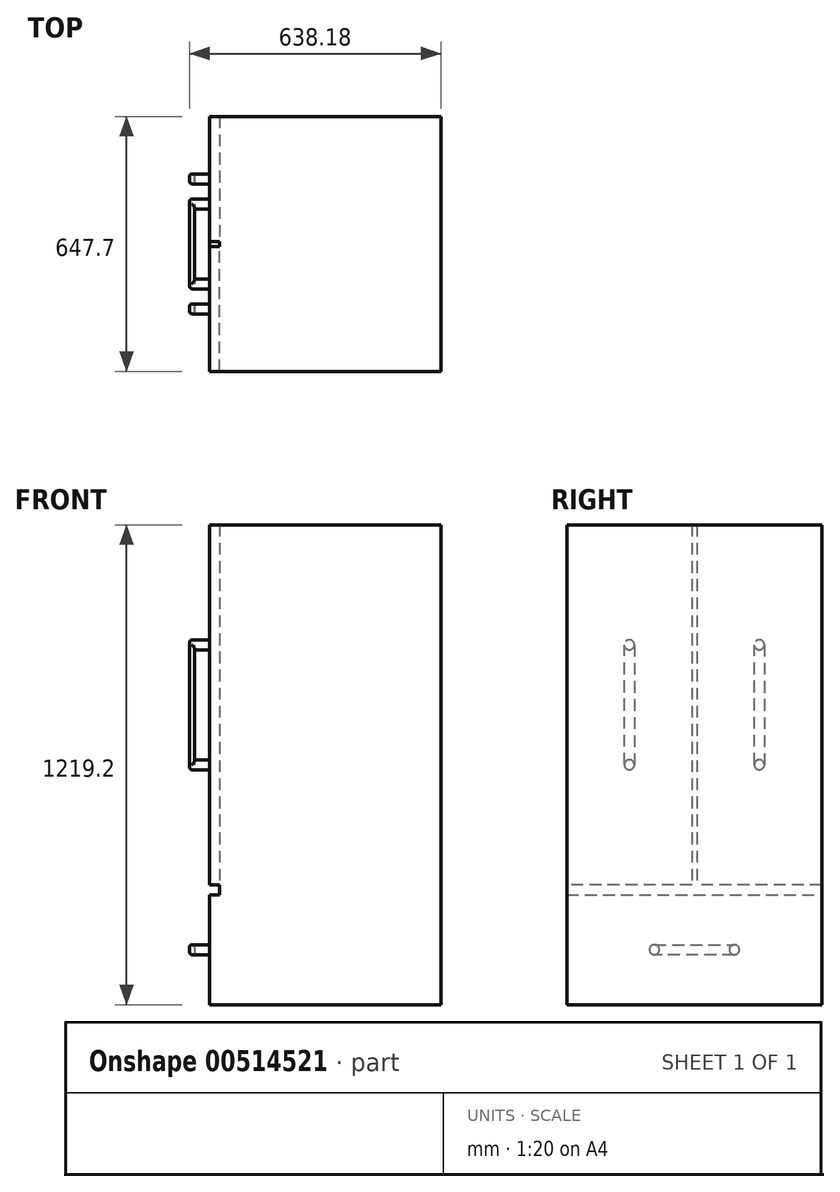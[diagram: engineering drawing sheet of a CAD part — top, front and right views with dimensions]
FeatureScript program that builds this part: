
annotation { "Feature Type Name" : "Feature", "Feature Type Description" : "" }
export const myFeature = defineFeature(function(context is Context, id is Id, definition is map)
    precondition{}
    {
        {
            var Q0;
            Q0=qCreatedBy(makeId("Top.planeOp"),FACE);
            var sketch = newSketch(context, id + "F0", { "sketchPlane" : qUnion([Q0])});
            skLineSegment(sketch, "E0.bottom", {"start": v(293.69, 323.85) * mm, "end": v(-293.69, 323.85) * mm});
            skLineSegment(sketch, "E0.top", {"start": v(293.69, -323.85) * mm, "end": v(-293.69, -323.85) * mm});
            skLineSegment(sketch, "E0.left", {"start": v(293.69, 323.85) * mm, "end": v(293.69, -323.85) * mm});
            skLineSegment(sketch, "E0.right", {"start": v(-293.69, 323.85) * mm, "end": v(-293.69, -323.85) * mm});
            skPoint(sketch, "E0.middle", {"position": v(0, 0) * mm});
            skSolve(sketch);
        }
        {
            var Q0;
            Q0=makeQuery(id+"F0.imprint","IMPRINT",FACE,{"disambiguationData":[TD([[makeQuery(id+"F0.imprint","IMPRINT",EDGE,{"derivedFrom":sQuery(id+"F0.wireOp",EDGE,"E0.bottom")}),1.0]])]});
            extrude(context, id + "F1", {"entities" : qUnion([Q0]), "depth" : 1219.2 * mm, "offsetDistance" : 25.4 * mm});
        }
        {
            var Q0;
            Q0=makeQuery(id+"F1.opExtrude","SWEPT_FACE",FACE,{"disambiguationData":[OSD([sQuery(id+"F0.wireOp",EDGE,"E0.right")])]});
            var sketch = newSketch(context, id + "F2", { "sketchPlane" : qUnion([Q0])});
            skLineSegment(sketch, "E1.bottom", {"start": v(-323.85, 1219.2) * mm, "end": v(-6.35, 1219.2) * mm});
            skLineSegment(sketch, "E1.top", {"start": v(-323.85, 304.8) * mm, "end": v(-6.35, 304.8) * mm});
            skLineSegment(sketch, "E1.left", {"start": v(-323.85, 1219.2) * mm, "end": v(-323.85, 304.8) * mm});
            skLineSegment(sketch, "E1.right", {"start": v(-6.35, 1219.2) * mm, "end": v(-6.35, 304.8) * mm});
            skLineSegment(sketch, "E2.bottom", {"start": v(6.35, 1219.2) * mm, "end": v(323.85, 1219.2) * mm});
            skLineSegment(sketch, "E2.top", {"start": v(6.35, 304.8) * mm, "end": v(323.85, 304.8) * mm});
            skLineSegment(sketch, "E2.left", {"start": v(6.35, 1219.2) * mm, "end": v(6.35, 304.8) * mm});
            skLineSegment(sketch, "E2.right", {"start": v(323.85, 1219.2) * mm, "end": v(323.85, 304.8) * mm});
            skLineSegment(sketch, "E3.bottom", {"start": v(323.85, 279.4) * mm, "end": v(-323.85, 279.4) * mm});
            skLineSegment(sketch, "E3.top", {"start": v(323.85, 50.8) * mm, "end": v(-323.85, 50.8) * mm});
            skLineSegment(sketch, "E3.left", {"start": v(323.85, 279.4) * mm, "end": v(323.85, 50.8) * mm});
            skLineSegment(sketch, "E3.right", {"start": v(-323.85, 279.4) * mm, "end": v(-323.85, 50.8) * mm});
            skSolve(sketch);
        }
        {
            var Q0;
            {var subQ6=sQuery(id+"F2.wireOp",EDGE,"E1.top");Q0=makeQuery(id+"F2.imprint","IMPRINT",FACE,{"disambiguationData":[TD([[makeQuery(id+"F2.imprint","IMPRINT",EDGE,{"derivedFrom":subQ6}),-1.0]])]});}
            extrude(context, id + "F3", {"entities" : qUnion([Q0]), "operationType" : NewBodyOperationType.REMOVE, "oppositeDirection" : true, "depth" : 25.4 * mm, "offsetDistance" : 25.4 * mm});
        }
        {
            var Q0;
            {var subQ1=sQuery(id+"F0.wireOp",EDGE,"E0.right");Q0=makeQuery(id+"F3.boolean.opBoolean","SPLIT",FACE,{"disambiguationData":[TD([makeQuery(id+"F3.opExtrude","SWEPT_FACE",FACE,{"disambiguationData":[OSD([sQuery(id+"F2.wireOp",EDGE,"E1.top")])]})])],"derivedFrom":makeQuery(id+"F1.opExtrude","SWEPT_FACE",FACE,{"disambiguationData":[OSD([subQ1])]})});}
            var sketch = newSketch(context, id + "F4", { "sketchPlane" : qUnion([Q0])});
            skCircle(sketch, "E4", {"center": v(-165.1, 609.6) * mm, "radius": 12.7 * mm});
            skCircle(sketch, "E5", {"center": v(-165.1, 914.4) * mm, "radius": 12.7 * mm});
            skCircle(sketch, "E6", {"center": v(165.1, 914.4) * mm, "radius": 12.7 * mm});
            skCircle(sketch, "E7", {"center": v(165.1, 609.6) * mm, "radius": 12.7 * mm});
            skCircle(sketch, "E8", {"center": v(101.6, 139.7) * mm, "radius": 12.7 * mm});
            skCircle(sketch, "E9", {"center": v(-101.6, 139.7) * mm, "radius": 12.7 * mm});
            skLineSegment(sketch, "E10", {"start": v(-165.1, 914.4) * mm, "end": v(-165.1, 1219.2) * mm});
            skLineSegment(sketch, "E11", {"start": v(-6.35, 1219.2) * mm, "end": v(-165.1, 1219.2) * mm});
            skLineSegment(sketch, "E12", {"start": v(-323.85, 1219.2) * mm, "end": v(-165.1, 1219.2) * mm});
            skLineSegment(sketch, "E13", {"start": v(-101.6, 139.7) * mm, "end": v(-101.6, 279.4) * mm});
            skLineSegment(sketch, "E14", {"start": v(-101.6, 139.7) * mm, "end": v(-101.6, 0) * mm});
            skSolve(sketch);
        }
        {
            var Q0;
            Q0 = qSketchRegion(id + "F4", true);
            extrude(context, id + "F5", {"entities" : qUnion([Q0]), "operationType" : NewBodyOperationType.ADD, "depth" : 50.8 * mm, "offsetDistance" : 25.4 * mm});
        }
        {
            var Q0;
            Q0=makeQuery(id+"F5.opExtrude","CAP_FACE",FACE,{"disambiguationData":[OSD([sQuery(id+"F4.wireOp",EDGE,"E5")])],"isStart":false});
            var sketch = newSketch(context, id + "F6", { "sketchPlane" : qUnion([Q0])});
            skLineSegment(sketch, "E15.bottom", {"start": v(-177.8, 914.4) * mm, "end": v(-152.4, 914.4) * mm});
            skLineSegment(sketch, "E15.top", {"start": v(-177.8, 609.6) * mm, "end": v(-152.4, 609.6) * mm});
            skLineSegment(sketch, "E15.left", {"start": v(-177.8, 914.4) * mm, "end": v(-177.8, 609.6) * mm});
            skLineSegment(sketch, "E15.right", {"start": v(-152.4, 914.4) * mm, "end": v(-152.4, 609.6) * mm});
            skLineSegment(sketch, "E16.bottom", {"start": v(152.4, 914.4) * mm, "end": v(177.8, 914.4) * mm});
            skLineSegment(sketch, "E16.top", {"start": v(152.4, 609.6) * mm, "end": v(177.8, 609.6) * mm});
            skLineSegment(sketch, "E16.left", {"start": v(152.4, 914.4) * mm, "end": v(152.4, 609.6) * mm});
            skLineSegment(sketch, "E16.right", {"start": v(177.8, 914.4) * mm, "end": v(177.8, 609.6) * mm});
            skLineSegment(sketch, "E17.bottom", {"start": v(-101.6, 152.4) * mm, "end": v(101.6, 152.4) * mm});
            skLineSegment(sketch, "E17.top", {"start": v(-101.6, 127) * mm, "end": v(101.6, 127) * mm});
            skLineSegment(sketch, "E17.left", {"start": v(-101.6, 152.4) * mm, "end": v(-101.6, 127) * mm});
            skLineSegment(sketch, "E17.right", {"start": v(101.6, 152.4) * mm, "end": v(101.6, 127) * mm});
            skSolve(sketch);
        }
        {
            var Q0;
            Q0=makeQuery(id+"F6.imprint","IMPRINT",FACE,{"disambiguationData":[TD([[makeQuery(id+"F6.imprint","IMPRINT",EDGE,{"derivedFrom":sQuery(id+"F6.wireOp",EDGE,"E17.bottom")}),-1.0]])]});
            var Q1;
            Q1=makeQuery(id+"F6.imprint","IMPRINT",FACE,{"disambiguationData":[TD([[makeQuery(id+"F6.imprint","IMPRINT",EDGE,{"derivedFrom":sQuery(id+"F6.wireOp",EDGE,"E16.bottom")}),-1.0]])]});
            var Q2;
            Q2=makeQuery(id+"F6.imprint","IMPRINT",FACE,{"disambiguationData":[TD([[makeQuery(id+"F6.imprint","IMPRINT",EDGE,{"derivedFrom":sQuery(id+"F6.wireOp",EDGE,"E15.top")}),1.0]])]});
            extrude(context, id + "F7", {"entities" : qUnion([Q0, Q1, Q2]), "operationType" : NewBodyOperationType.ADD, "oppositeDirection" : true, "depth" : 12.7 * mm, "offsetDistance" : 25.4 * mm});
        }
        {
            var Q0;
            Q0=makeQuery(id+"F7.opExtrude","SWEPT_FACE",FACE,{"disambiguationData":[OSD([sQuery(id+"F6.wireOp",EDGE,"E15.right")])]});
            var Q1;
            Q1=makeQuery(id+"F7.opExtrude","SWEPT_FACE",FACE,{"disambiguationData":[OSD([sQuery(id+"F6.wireOp",EDGE,"E16.right")])]});
            var Q2;
            Q2=makeQuery(id+"F7.opExtrude","SWEPT_FACE",FACE,{"disambiguationData":[OSD([sQuery(id+"F6.wireOp",EDGE,"E17.bottom")])]});
            fillet(context, id + "F8", {"entities" : qUnion([Q0, Q1, Q2]), "radius" : 6.35 * mm, "tangentPropagation" : true, "allowEdgeOverflow" : false});
        }
    });
